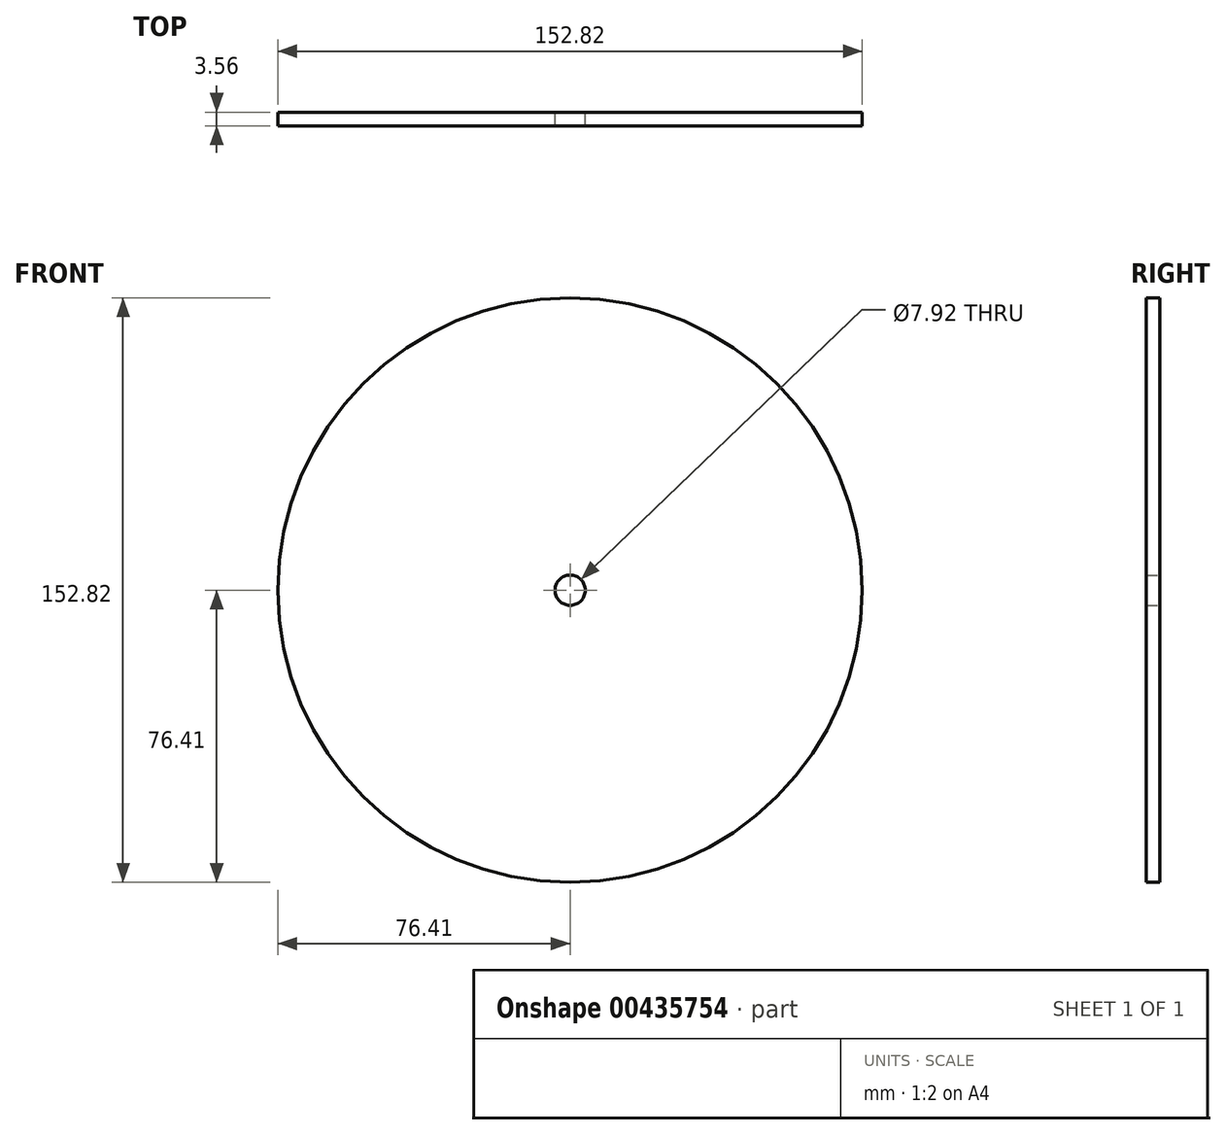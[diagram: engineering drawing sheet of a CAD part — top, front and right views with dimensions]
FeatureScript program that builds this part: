
annotation { "Feature Type Name" : "Feature", "Feature Type Description" : "" }
export const myFeature = defineFeature(function(context is Context, id is Id, definition is map)
    precondition{}
    {
        {
            var Q0;
            Q0=qCreatedBy(makeId("Front.planeOp"),FACE);
            var sketch = newSketch(context, id + "F0", { "sketchPlane" : qUnion([Q0])});
            skCircle(sketch, "E0", {"center": v(0, 0) * mm, "radius": 76.41 * mm});
            skLineSegment(sketch, "E1", {"start": v(50.6, 57.26) * mm, "end": v(-50.27, -57.55) * mm});
            skLineSegment(sketch, "E2", {"start": v(-49, 58.63) * mm, "end": v(49.05, -58.6) * mm});
            skSolve(sketch);
        }
        {
            var Q0;
            Q0 = qSketchRegion(id + "F0", true);
            extrude(context, id + "F1", {"entities" : qUnion([Q0]), "depth" : 3.56 * mm});
        }
        {
            var Q0;
            Q0=sQuery(id+"F0.wireOp",VERTEX,"E0.center");
            var Q1;
            Q1=makeQuery(id+"F1.opExtrude","SWEPT_BODY",BODY,{"disambiguationData":[OSD([sQuery(id+"F0.wireOp",EDGE,"E0")])]});
            hole(context, id + "F2", {"style" : HoleStyle.SIMPLE, "endStyle" : HoleEndStyle.THROUGH, "oppositeDirection" : true, "holeDiameter" : 7.92 * mm, "isTappedThrough" : true, "tappedDepth" : 12.7 * mm, "tapClearance" : 3, "locations" : qUnion([Q0]), "scope" : qUnion([Q1])});
        }
    });
